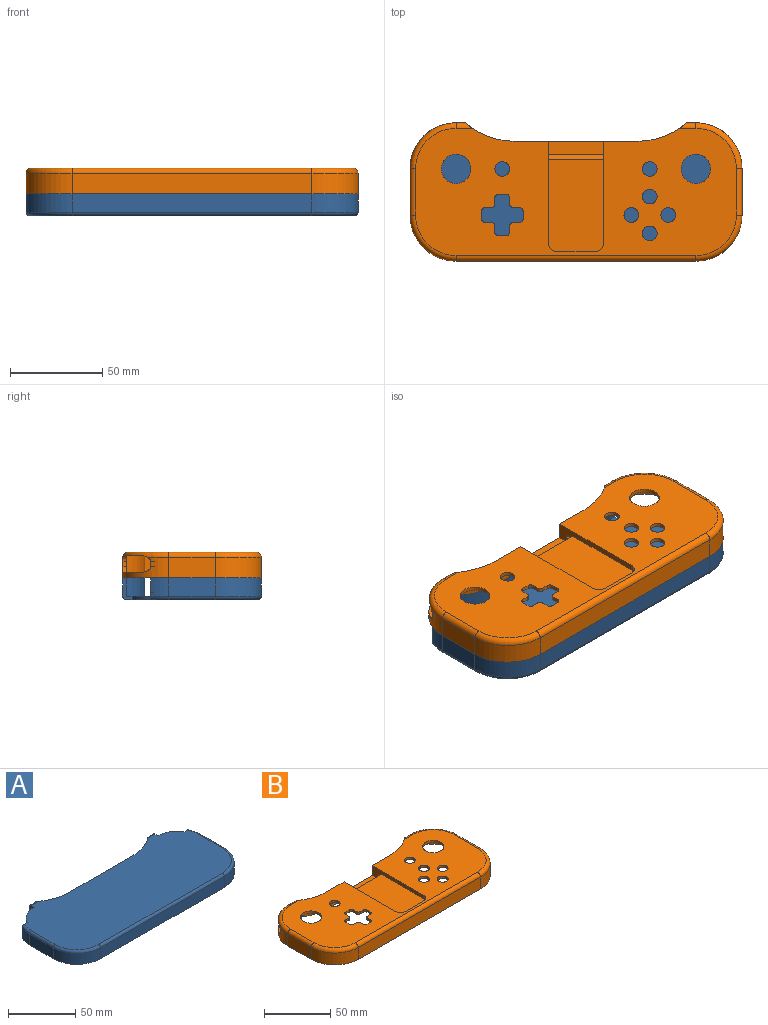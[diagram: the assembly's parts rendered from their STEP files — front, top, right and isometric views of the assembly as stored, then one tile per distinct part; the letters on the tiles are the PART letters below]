
ASSEMBLY  parts=2 mates=1
PART A: 46 faces, bbox 184.1x77.1x12 mm
  f0: plane 176x71mm, normal (0,0,1), area 11102mm2, adj f2,f10,f23,f24,f25,f26,f29,f30
  f1: plane 172x69mm, normal (0,0,-1), area 10321.5mm2, adj f20,f21,f22,f23,f24,f27,f28,f37
  f2: torus R=23mm, axis (0,0,1), area 31.7mm2, adj f0,f14,f35,f37
  f3: plane 180x59.8mm, normal (0,0,-1), area 537.1mm2, adj f5,f6,f8,f11,f12,f13,f14,f15
  f4: plane 130x12mm, normal (0,0,-1), area 282mm2, adj f7,f9,f10,f20,f21,f22,f23,f24
  f5: plane 25x10mm, normal (1,0,0), area 250mm2, adj f3,f11,f14,f35
  f6: plane 25x10mm, normal (-1,0,0), area 250mm2, adj f3,f12,f13,f31
  f7: plane 10x5mm, normal (0,1,0), area 50mm2, adj f4,f23,f25,f36
  f8: plane 130x10mm, normal (0,-1,0), area 1300mm2, adj f3,f11,f12,f33
  f9: plane 10x5mm, normal (0,1,0), area 50mm2, adj f4,f24,f26,f29
  f10: plane 67.09x12mm, normal (0,1,0), area 805mm2, adj f0,f4,f25,f26
  f11: cylinder r=25mm len=25mm, axis (0,0,1), area 392.7mm2, adj f3,f5,f8,f34
  f12: cylinder r=25mm len=25mm, axis (0,0,1), area 392.7mm2, adj f3,f6,f8,f32
  f13: cylinder r=25mm len=10mm, axis (0,0,1), area 100.7mm2, adj f3,f6,f19,f30,f40
  f14: cylinder r=25mm len=10mm, axis (0,0,1), area 100.7mm2, adj f2,f3,f5,f15,f37
  f15: plane 34.8x8mm, normal (-1,0,0), area 278.4mm2, adj f3,f14,f16,f45
  f16: cylinder r=23mm len=23mm, axis (0,0,-1), area 289mm2, adj f3,f15,f17,f44
  f17: plane 130x8mm, normal (0,1,0), area 1040mm2, adj f3,f16,f18,f43
  f18: cylinder r=23mm len=23mm, axis (0,0,-1), area 289mm2, adj f3,f17,f19,f42
  f19: plane 34.8x8mm, normal (1,0,0), area 278.4mm2, adj f3,f13,f18,f41
  f20: plane 10x4.17mm, normal (0,-1,0), area 41.7mm2, adj f1,f4,f24,f27
  f21: plane 70.28x10mm, normal (0,-1,0), area 702.8mm2, adj f1,f4,f27,f28
  f22: plane 10x4.17mm, normal (0,-1,0), area 41.7mm2, adj f1,f4,f23,f28
  f23: plane 12x5mm, normal (1,0,0), area 29.1mm2, adj f0,f1,f4,f7,f22,f36,f38
  f24: plane 12x5mm, normal (-1,0,0), area 29.1mm2, adj f0,f1,f4,f9,f20,f29,f39
  f25: cylinder r=40mm len=26.46mm, axis (0,0,1), area 345.6mm2, adj f0,f4,f7,f10,f36
  f26: cylinder r=40mm len=26.46mm, axis (0,0,-1), area 345.6mm2, adj f0,f4,f9,f10,f29
  f27: cylinder r=38mm len=25.69mm, axis (0,0,1), area 282.1mm2, adj f1,f4,f20,f21
  f28: cylinder r=38mm len=25.69mm, axis (0,0,-1), area 282.1mm2, adj f1,f4,f21,f22
  f29: cylinder r=2mm len=7.46mm, axis (1,0,0), area 18.4mm2, adj f0,f9,f24,f26
  f30: torus R=23mm, axis (0,0,1), area 31.7mm2, adj f0,f13,f31,f40
  f31: cylinder r=2mm len=25mm, axis (0,1,0), area 78.5mm2, adj f0,f6,f30,f32
  f32: torus R=23mm, axis (0,0,1), area 119.8mm2, adj f0,f12,f31,f33
  f33: cylinder r=2mm len=130mm, axis (1,0,0), area 408.4mm2, adj f0,f8,f32,f34
  f34: torus R=23mm, axis (0,0,1), area 119.8mm2, adj f0,f11,f33,f35
  f35: cylinder r=2mm len=25mm, axis (0,-1,0), area 78.5mm2, adj f0,f2,f5,f34
  f36: cylinder r=2mm len=7.46mm, axis (1,0,0), area 18.4mm2, adj f0,f7,f23,f25
  f37: plane 5.57x4mm, normal (0,1,0), area 11.1mm2, adj f0,f1,f2,f14,f38,f45
  f38: cylinder r=20mm len=17.44mm, axis (0,0,-1), area 42.4mm2, adj f0,f1,f23,f37
  f39: cylinder r=20mm len=17.44mm, axis (0,0,-1), area 42.4mm2, adj f0,f1,f24,f40
  f40: plane 5.57x4mm, normal (0,1,0), area 11.1mm2, adj f0,f1,f13,f30,f39,f41
  f41: cylinder r=2mm len=34.8mm, axis (0,1,0), area 109.3mm2, adj f1,f19,f40,f42
  f42: torus R=21mm, axis (0,0,-1), area 109.9mm2, adj f1,f18,f41,f43
  f43: cylinder r=2mm len=130mm, axis (-1,0,0), area 408.4mm2, adj f1,f17,f42,f44
  f44: torus R=21mm, axis (0,0,-1), area 109.9mm2, adj f1,f16,f43,f45
  f45: cylinder r=2mm len=34.8mm, axis (0,-1,0), area 109.3mm2, adj f1,f15,f37,f44
PART B: 107 faces, bbox 184.1x79.1x14 mm
  f0: plane 67.09x14mm, normal (0,1,0), area 669.2mm2, adj f3,f34,f64,f65,f79,f81,f98
  f1: plane 17.64x12mm, normal (0,-1,0), area 211.7mm2, adj f34,f40,f67,f78
  f2: plane 46x35mm, normal (0,0,-1), area 1610mm2, adj f43,f77,f78,f102
  f3: plane 174x69mm, normal (0,0,1), area 8118.4mm2, adj f0,f11,f12,f13,f14,f15,f16,f17
  f4: plane 69.65x67.5mm, normal (0,0,-1), area 3576mm2, adj f5,f11,f12,f13,f14,f15,f16,f17
  f5: plane 17.64x12mm, normal (0,-1,0), area 211.7mm2, adj f4,f34,f66,f77
  f6: cylinder r=3mm len=47.5mm, axis (-1,0,0), area 223.8mm2, adj f40,f43,f56,f78
  f7: cylinder r=25mm len=2mm, axis (0,0,1), area 0.5mm2, adj f33,f59,f69
  f8: cylinder r=25mm len=25mm, axis (0,0,1), area 205.8mm2, adj f32,f34,f36,f45,f51,f53,f61,f62
  f9: cylinder r=25mm len=25mm, axis (0,0,1), area 205.8mm2, adj f31,f33,f34,f41,f49,f57,f58,f60
  f10: cylinder r=23mm len=23mm, axis (0,0,-1), area 124.1mm2, adj f34,f41,f48,f49,f58,f60
  f11: plane 4x2mm, normal (-1,0,0), area 8mm2, adj f3,f4,f85,f96
  f12: plane 3.31x2mm, normal (0,1,0), area 6.6mm2, adj f3,f4,f85,f86
  f13: plane 3.31x2mm, normal (-1,0,0), area 6.6mm2, adj f3,f4,f86,f87
  f14: plane 4x2mm, normal (0,1,0), area 8mm2, adj f3,f4,f87,f88
  f15: plane 3.31x2mm, normal (1,0,0), area 6.6mm2, adj f3,f4,f88,f89
  f16: plane 3.31x2mm, normal (0,1,0), area 6.6mm2, adj f3,f4,f89,f90
  f17: plane 4x2mm, normal (1,0,0), area 8mm2, adj f3,f4,f90,f91
  f18: plane 3.31x2mm, normal (0,-1,0), area 6.6mm2, adj f3,f4,f91,f92
  f19: plane 3.31x2mm, normal (1,0,0), area 6.6mm2, adj f3,f4,f92,f93
  f20: plane 4x2mm, normal (0,-1,0), area 8mm2, adj f3,f4,f93,f94
  f21: plane 3.31x2mm, normal (-1,0,0), area 6.6mm2, adj f3,f4,f94,f95
  f22: cylinder r=8mm len=16mm, axis (0,0,-1), area 100.5mm2, adj f3,f4
  f23: cylinder r=4mm len=8mm, axis (0,0,-1), area 50.3mm2, adj f3,f40
  f24: cylinder r=4mm len=8mm, axis (0,0,-1), area 50.3mm2, adj f3,f4
  f25: cylinder r=4mm len=8mm, axis (0,0,-1), area 50.3mm2, adj f3,f40
  f26: cylinder r=4mm len=8mm, axis (0,0,-1), area 50.3mm2, adj f3,f40
  f27: cylinder r=4mm len=8mm, axis (0,0,-1), area 50.3mm2, adj f3,f40
  f28: cylinder r=4mm len=8mm, axis (0,0,-1), area 50.3mm2, adj f3,f40
  f29: cylinder r=8mm len=16mm, axis (0,0,-1), area 100.5mm2, adj f3,f40
  f30: plane 3.31x2mm, normal (0,-1,0), area 6.6mm2, adj f3,f4,f95,f96
  f31: plane 25x11mm, normal (1,0,0), area 275mm2, adj f9,f34,f37,f70
  f32: plane 25x11mm, normal (-1,0,0), area 275mm2, adj f8,f34,f38,f74
  f33: plane 11x5mm, normal (0,1,0), area 55mm2, adj f7,f9,f34,f50,f64,f68
  f34: plane 180x75mm, normal (0,0,-1), area 1143.7mm2, adj f0,f1,f5,f8,f9,f10,f31,f32
  f35: plane 130x11mm, normal (0,-1,0), area 1430mm2, adj f34,f37,f38,f72
  f36: plane 11x5mm, normal (0,1,0), area 55mm2, adj f8,f34,f39,f52,f65,f76
  f37: cylinder r=25mm len=25mm, axis (0,0,1), area 432mm2, adj f31,f34,f35,f71
  f38: cylinder r=25mm len=25mm, axis (0,0,1), area 432mm2, adj f32,f34,f35,f73
  f39: cylinder r=25mm len=2mm, axis (0,0,1), area 0.5mm2, adj f36,f63,f75
  f40: plane 69.65x67.5mm, normal (0,0,-1), area 3669.5mm2, adj f1,f6,f23,f25,f26,f27,f28,f29
  f41: plane 34.8x9mm, normal (-1,0,0), area 254.4mm2, adj f9,f10,f34,f42,f57,f58
  f42: cylinder r=23mm len=23mm, axis (0,0,-1), area 325.2mm2, adj f34,f41,f43,f56
  f43: plane 130x9mm, normal (0,1,0), area 1170mm2, adj f2,f6,f34,f42,f44,f55
  f44: cylinder r=23mm len=23mm, axis (0,0,-1), area 325.2mm2, adj f34,f43,f45,f54
  f45: plane 34.8x9mm, normal (1,0,0), area 254.4mm2, adj f8,f34,f44,f46,f53,f61
  f46: cylinder r=23mm len=23mm, axis (0,0,-1), area 124.1mm2, adj f34,f45,f47,f51,f61,f62
  f47: plane 12x7.17mm, normal (0,-1,0), area 52mm2, adj f4,f34,f46,f52,f63,f66
  f48: plane 12x7.17mm, normal (0,-1,0), area 52mm2, adj f10,f34,f40,f50,f59,f67
  f49: plane 17x13.46mm, normal (0,0,1), area 41.3mm2, adj f9,f10,f58,f60
  f50: plane 3x2mm, normal (1,0,0), area 6mm2, adj f33,f48,f59,f60
  f51: plane 17x13.46mm, normal (0,0,1), area 41.3mm2, adj f8,f46,f61,f62
  f52: plane 3x2mm, normal (-1,0,0), area 6mm2, adj f36,f47,f62,f63
  f53: cylinder r=3mm len=39.71mm, axis (0,1,0), area 173.5mm2, adj f4,f8,f45,f54,f75
  f54: torus R=20mm, axis (0,0,-1), area 162.2mm2, adj f4,f44,f53,f55
  f55: cylinder r=3mm len=47.5mm, axis (-1,0,0), area 223.8mm2, adj f4,f43,f54,f77
  f56: torus R=20mm, axis (0,0,-1), area 162.2mm2, adj f6,f40,f42,f57
  f57: cylinder r=3mm len=39.71mm, axis (0,-1,0), area 173.5mm2, adj f9,f40,f41,f56,f69
  f58: cylinder r=3mm len=15mm, axis (0,-1,0), area 27.3mm2, adj f9,f10,f41,f49
  f59: cylinder r=3mm len=3mm, axis (0,1,0), area 9mm2, adj f7,f40,f48,f50,f69
  f60: cylinder r=3mm len=3mm, axis (0,1,0), area 9.4mm2, adj f9,f10,f49,f50
  f61: cylinder r=3mm len=15mm, axis (0,1,0), area 27.3mm2, adj f8,f45,f46,f51
  f62: cylinder r=3mm len=3mm, axis (0,1,0), area 9.4mm2, adj f8,f46,f51,f52
  f63: cylinder r=3mm len=3mm, axis (0,-1,0), area 9mm2, adj f4,f39,f47,f52,f75
  f64: cylinder r=40mm len=26.46mm, axis (0,0,1), area 401.7mm2, adj f0,f3,f33,f34,f68
  f65: cylinder r=40mm len=26.46mm, axis (0,0,-1), area 401.7mm2, adj f0,f3,f34,f36,f76
  f66: cylinder r=38mm len=25.69mm, axis (0,0,1), area 338.5mm2, adj f4,f5,f34,f47
  f67: cylinder r=38mm len=25.69mm, axis (0,0,-1), area 338.5mm2, adj f1,f34,f40,f48
  f68: cylinder r=3mm len=8.85mm, axis (1,0,0), area 29.8mm2, adj f3,f33,f64,f69
  f69: torus R=22mm, axis (0,0,1), area 151.9mm2, adj f3,f7,f9,f40,f57,f59,f68,f70
  f70: cylinder r=3mm len=25mm, axis (0,-1,0), area 117.8mm2, adj f3,f31,f69,f71
  f71: torus R=22mm, axis (0,0,1), area 177mm2, adj f3,f37,f70,f72
  f72: cylinder r=3mm len=130mm, axis (1,0,0), area 612.6mm2, adj f3,f35,f71,f73
  f73: torus R=22mm, axis (0,0,1), area 177mm2, adj f3,f38,f72,f74
  f74: cylinder r=3mm len=25mm, axis (0,1,0), area 117.8mm2, adj f3,f32,f73,f75
  f75: torus R=22mm, axis (0,0,1), area 151.9mm2, adj f3,f4,f8,f39,f53,f63,f74,f76
  f76: cylinder r=3mm len=8.85mm, axis (1,0,0), area 29.8mm2, adj f3,f36,f65,f75
  f77: plane 61x12mm, normal (-1,0,0), area 268.5mm2, adj f2,f4,f5,f34,f55,f101,f102
  f78: plane 61x12mm, normal (1,0,0), area 268.5mm2, adj f1,f2,f6,f34,f40,f100,f102
  f79: plane 55x9mm, normal (1,0,0), area 216mm2, adj f0,f3,f82,f83,f97,f98,f99,f101
  f80: plane 20x3mm, normal (0,1,0), area 60mm2, adj f3,f82,f83,f84
  f81: plane 55x9mm, normal (-1,0,0), area 216mm2, adj f0,f3,f82,f84,f97,f98,f99,f100
  f82: plane 50x30mm, normal (0,0,1), area 1489.3mm2, adj f79,f80,f81,f83,f84,f97
  f83: cylinder r=5mm len=5mm, axis (0,0,1), area 23.6mm2, adj f3,f79,f80,f82
  f84: cylinder r=5mm len=5mm, axis (0,0,-1), area 23.6mm2, adj f3,f80,f81,f82
  f85: cylinder r=2mm len=2mm, axis (0,0,-1), area 6.3mm2, adj f3,f4,f11,f12
  f86: cylinder r=2mm len=2mm, axis (0,0,1), area 6.3mm2, adj f3,f4,f12,f13
  f87: cylinder r=2mm len=2mm, axis (0,0,1), area 6.3mm2, adj f3,f4,f13,f14
  f88: cylinder r=2mm len=2mm, axis (0,0,-1), area 6.3mm2, adj f3,f4,f14,f15
  f89: cylinder r=2mm len=2mm, axis (0,0,-1), area 6.3mm2, adj f3,f4,f15,f16
  f90: cylinder r=2mm len=2mm, axis (0,0,1), area 6.3mm2, adj f3,f4,f16,f17
  f91: cylinder r=2mm len=2mm, axis (0,0,-1), area 6.3mm2, adj f3,f4,f17,f18
  f92: cylinder r=2mm len=2mm, axis (0,0,1), area 6.3mm2, adj f3,f4,f18,f19
  f93: cylinder r=2mm len=2mm, axis (0,0,1), area 6.3mm2, adj f3,f4,f19,f20
  f94: cylinder r=2mm len=2mm, axis (0,0,-1), area 6.3mm2, adj f3,f4,f20,f21
  f95: cylinder r=2mm len=2mm, axis (0,0,-1), area 6.3mm2, adj f3,f4,f21,f30
  f96: cylinder r=2mm len=2mm, axis (0,0,1), area 6.3mm2, adj f3,f4,f11,f30
  f97: plane 30x3mm, normal (0,1,0), area 90mm2, adj f79,f81,f82,f99
  f98: plane 30x7mm, normal (0,0,1), area 210mm2, adj f0,f79,f81,f99
  f99: cylinder r=3mm len=30mm, axis (1,0,0), area 141.4mm2, adj f79,f81,f97,f98
  f100: cylinder r=1.5mm len=3mm, axis (1,0,0), area 23.6mm2, adj f78,f81
  f101: cylinder r=1.5mm len=3mm, axis (1,0,0), area 23.6mm2, adj f77,f79
  f102: plane 35x9mm, normal (0,-0.71,-0.71), area 445.5mm2, adj f2,f34,f77,f78
  f103: cone r=0mm half-angle=59deg, axis (0,0,-1), area 5.7mm2, adj f104
  f104: cylinder r=1.25mm len=3.5mm, axis (0,0,-1), area 27.5mm2, adj f34,f103
  f105: cone r=0mm half-angle=59deg, axis (0,0,-1), area 5.7mm2, adj f106
  f106: cylinder r=1.25mm len=3.5mm, axis (0,0,-1), area 27.5mm2, adj f34,f105
PLACE A rot(axis=(0,1,0),180deg) t=(0,-9.83,12)mm
PLACE B t=(0,-9.83,12)mm
MATE fastened B.f34 <-> A.f4  axis (0,0,-1) through (65,40.17,12)mm
